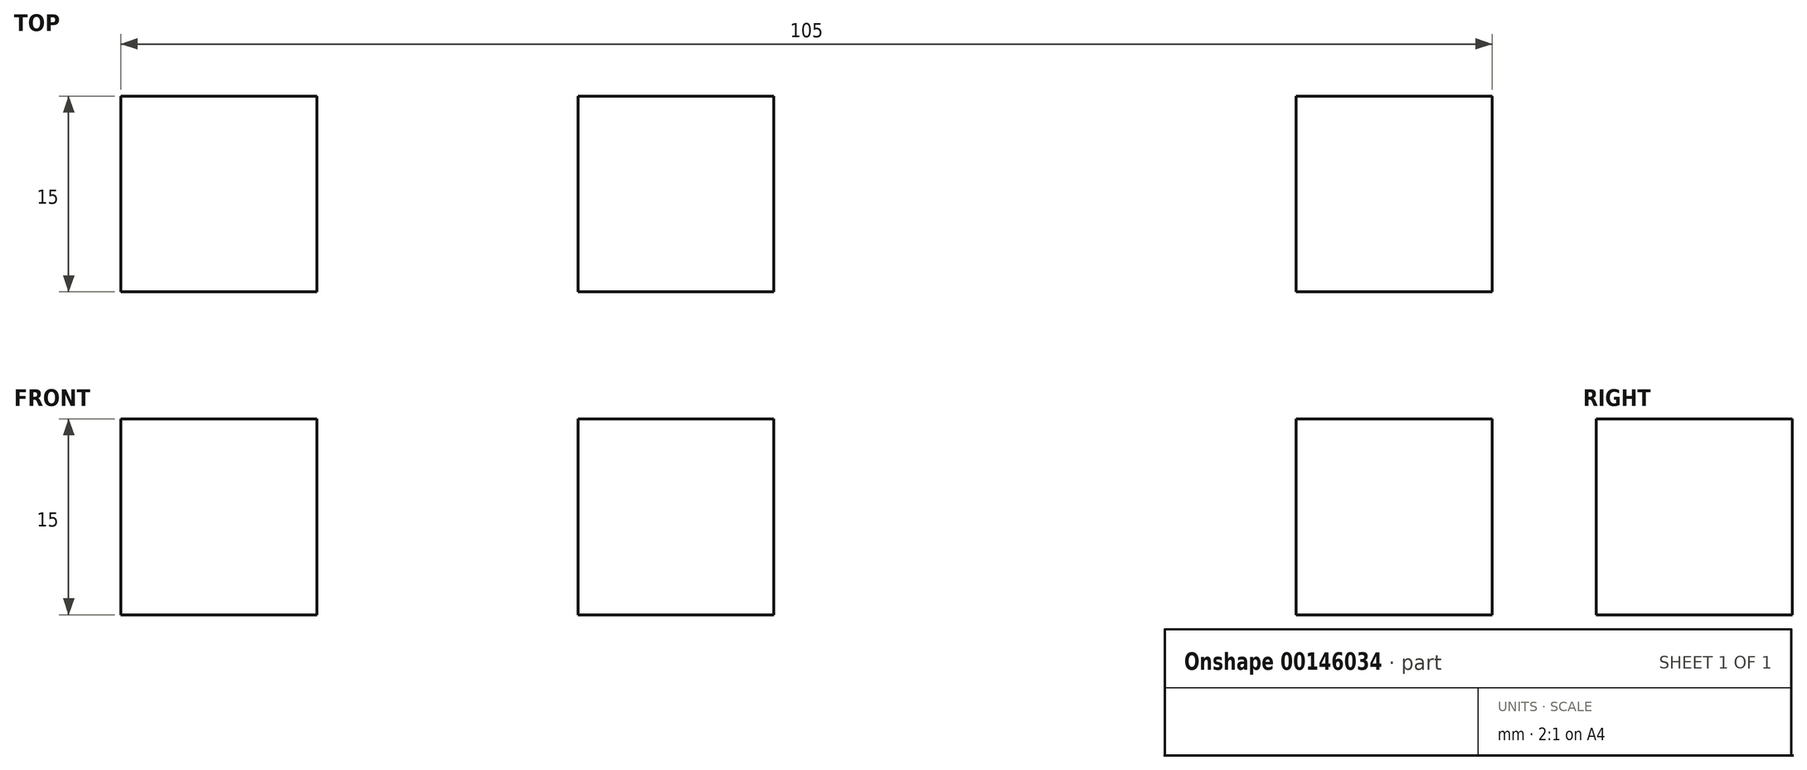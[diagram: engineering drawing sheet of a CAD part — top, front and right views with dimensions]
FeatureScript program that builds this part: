
annotation { "Feature Type Name" : "Feature", "Feature Type Description" : "" }
export const myFeature = defineFeature(function(context is Context, id is Id, definition is map)
    precondition{}
    {
        {
            var Q0;
            Q0=qCreatedBy(makeId("Top.planeOp"),FACE);
            var sketch = newSketch(context, id + "F0", { "sketchPlane" : qUnion([Q0])});
            skLineSegment(sketch, "E0.bottom", {"start": v(0, 0) * mm, "end": v(15, 0) * mm});
            skLineSegment(sketch, "E0.top", {"start": v(0, 15) * mm, "end": v(15, 15) * mm});
            skLineSegment(sketch, "E0.left", {"start": v(0, 0) * mm, "end": v(0, 15) * mm});
            skLineSegment(sketch, "E0.right", {"start": v(15, 0) * mm, "end": v(15, 15) * mm});
            skLineSegment(sketch, "E1.bottom", {"start": v(35, 0) * mm, "end": v(50, 0) * mm});
            skLineSegment(sketch, "E1.top", {"start": v(35, 15) * mm, "end": v(50, 15) * mm});
            skLineSegment(sketch, "E1.left", {"start": v(35, 0) * mm, "end": v(35, 15) * mm});
            skLineSegment(sketch, "E1.right", {"start": v(50, 0) * mm, "end": v(50, 15) * mm});
            skLineSegment(sketch, "E2.bottom", {"start": v(105, 0) * mm, "end": v(90, 0) * mm});
            skLineSegment(sketch, "E2.top", {"start": v(105, 15) * mm, "end": v(90, 15) * mm});
            skLineSegment(sketch, "E2.left", {"start": v(105, 0) * mm, "end": v(105, 15) * mm});
            skLineSegment(sketch, "E2.right", {"start": v(90, 0) * mm, "end": v(90, 15) * mm});
            skSolve(sketch);
        }
        {
            var Q0;
            Q0=makeQuery(id+"F0.imprint","IMPRINT",FACE,{"disambiguationData":[TD([[makeQuery(id+"F0.imprint","IMPRINT",EDGE,{"derivedFrom":sQuery(id+"F0.wireOp",EDGE,"E0.bottom")}),1.0]])]});
            var Q1;
            Q1=makeQuery(id+"F0.imprint","IMPRINT",FACE,{"disambiguationData":[TD([[makeQuery(id+"F0.imprint","IMPRINT",EDGE,{"derivedFrom":sQuery(id+"F0.wireOp",EDGE,"E1.bottom")}),1.0]])]});
            var Q2;
            Q2=makeQuery(id+"F0.imprint","IMPRINT",FACE,{"disambiguationData":[TD([[makeQuery(id+"F0.imprint","IMPRINT",EDGE,{"derivedFrom":sQuery(id+"F0.wireOp",EDGE,"E2.bottom")}),-1.0]])]});
            extrude(context, id + "F1", {"entities" : qUnion([Q0, Q1, Q2]), "depth" : 15 * mm});
        }
    });
